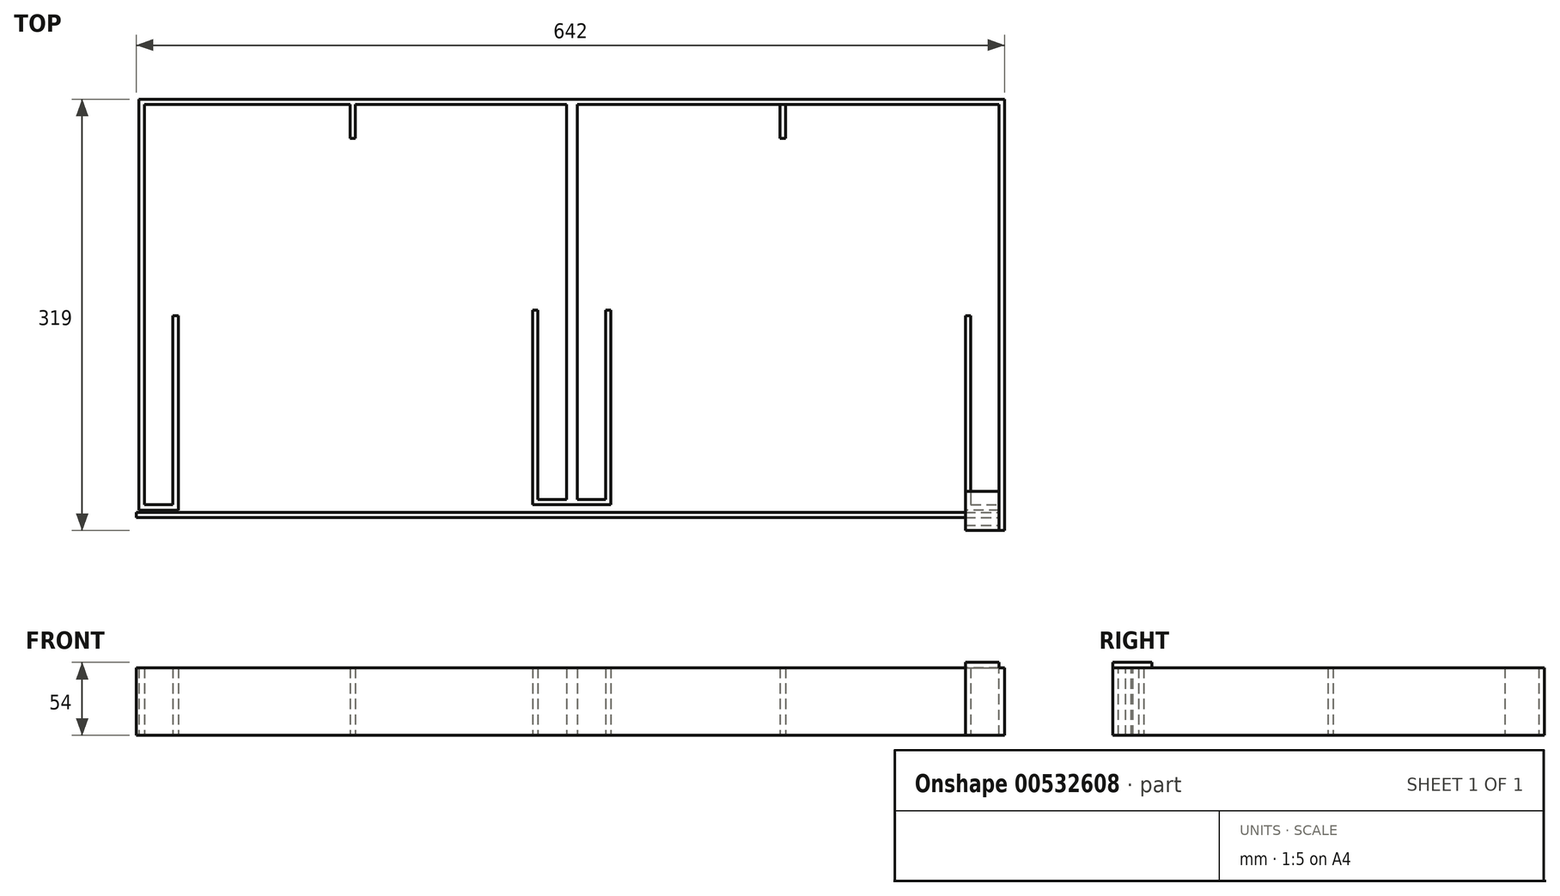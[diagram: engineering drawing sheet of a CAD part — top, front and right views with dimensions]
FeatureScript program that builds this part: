
annotation { "Feature Type Name" : "Feature", "Feature Type Description" : "" }
export const myFeature = defineFeature(function(context is Context, id is Id, definition is map)
    precondition{}
    {
        {
            var Q0;
            Q0=qCreatedBy(makeId("Front.planeOp"),FACE);
            var sketch = newSketch(context, id + "F0", { "sketchPlane" : qUnion([Q0])});
            skLineSegment(sketch, "E0.bottom", {"start": v(320, 25) * mm, "end": v(-320, 25) * mm});
            skLineSegment(sketch, "E0.top", {"start": v(320, -25) * mm, "end": v(-320, -25) * mm});
            skLineSegment(sketch, "E0.left", {"start": v(320, 25) * mm, "end": v(320, -25) * mm});
            skLineSegment(sketch, "E0.right", {"start": v(-320, 25) * mm, "end": v(-320, -25) * mm});
            skPoint(sketch, "E0.middle", {"position": v(0, 0) * mm});
            skSolve(sketch);
        }
        {
            var Q0;
            Q0=makeQuery(id+"F0.imprint","IMPRINT",FACE,{"disambiguationData":[TD([[makeQuery(id+"F0.imprint","IMPRINT",EDGE,{"derivedFrom":sQuery(id+"F0.wireOp",EDGE,"E0.bottom")}),1.0]])]});
            extrude(context, id + "F1", {"entities" : qUnion([Q0]), "depth" : 4 * mm, "offsetDistance" : 25 * mm});
        }
        {
            var Q0;
            Q0=makeQuery(id+"F1.opExtrude","CAP_FACE",FACE,{"disambiguationData":[OSD([sQuery(id+"F0.wireOp",EDGE,"E0.bottom"),sQuery(id+"F0.wireOp",EDGE,"E0.top"),sQuery(id+"F0.wireOp",EDGE,"E0.left"),sQuery(id+"F0.wireOp",EDGE,"E0.right")])],"isStart":false});
            var sketch = newSketch(context, id + "F2", { "sketchPlane" : qUnion([Q0])});
            skLineSegment(sketch, "E1.bottom", {"start": v(-320, 25) * mm, "end": v(-316, 25) * mm});
            skLineSegment(sketch, "E1.top", {"start": v(-320, -25) * mm, "end": v(-316, -25) * mm});
            skLineSegment(sketch, "E1.left", {"start": v(-320, 25) * mm, "end": v(-320, -25) * mm});
            skLineSegment(sketch, "E1.right", {"start": v(-316, 25) * mm, "end": v(-316, -25) * mm});
            skSolve(sketch);
        }
        {
            var Q0;
            Q0=qSketchRegion(id+"F2",true);
            extrude(context, id + "F3", {"entities" : qUnion([Q0]), "operationType" : NewBodyOperationType.ADD, "depth" : 300 * mm, "offsetDistance" : 25 * mm});
        }
        {
            var Q0;
            Q0=makeQuery(id+"F1.opExtrude","CAP_FACE",FACE,{"disambiguationData":[OSD([sQuery(id+"F0.wireOp",EDGE,"E0.bottom"),sQuery(id+"F0.wireOp",EDGE,"E0.top"),sQuery(id+"F0.wireOp",EDGE,"E0.left"),sQuery(id+"F0.wireOp",EDGE,"E0.right")])],"isStart":false});
            var sketch = newSketch(context, id + "F4", { "sketchPlane" : qUnion([Q0])});
            skLineSegment(sketch, "E2.bottom", {"start": v(320, -25) * mm, "end": v(316, -25) * mm});
            skLineSegment(sketch, "E2.top", {"start": v(320, 25) * mm, "end": v(316, 25) * mm});
            skLineSegment(sketch, "E2.left", {"start": v(320, -25) * mm, "end": v(320, 25) * mm});
            skLineSegment(sketch, "E2.right", {"start": v(316, -25) * mm, "end": v(316, 25) * mm});
            skSolve(sketch);
        }
        {
            var Q0;
            Q0=qSketchRegion(id+"F4",true);
            extrude(context, id + "F5", {"entities" : qUnion([Q0]), "operationType" : NewBodyOperationType.ADD, "depth" : 300 * mm, "offsetDistance" : 25 * mm});
        }
        {
            var Q0;
            Q0=makeQuery(id+"F3.opExtrude","SWEPT_FACE",FACE,{"disambiguationData":[OSD([sQuery(id+"F2.wireOp",EDGE,"E1.right")])]});
            var sketch = newSketch(context, id + "F6", { "sketchPlane" : qUnion([Q0])});
            skLineSegment(sketch, "E3.bottom", {"start": v(-304, 25) * mm, "end": v(-300, 25) * mm});
            skLineSegment(sketch, "E3.top", {"start": v(-304, -25) * mm, "end": v(-300, -25) * mm});
            skLineSegment(sketch, "E3.left", {"start": v(-304, 25) * mm, "end": v(-304, -25) * mm});
            skLineSegment(sketch, "E3.right", {"start": v(-300, 25) * mm, "end": v(-300, -25) * mm});
            skSolve(sketch);
        }
        {
            var Q0;
            Q0=qSketchRegion(id+"F6",true);
            extrude(context, id + "F7", {"entities" : qUnion([Q0]), "operationType" : NewBodyOperationType.ADD, "depth" : 25 * mm, "offsetDistance" : 25 * mm});
        }
        {
            var Q0;
            Q0=makeQuery(id+"F5.opExtrude","SWEPT_FACE",FACE,{"disambiguationData":[OSD([sQuery(id+"F4.wireOp",EDGE,"E2.right")])]});
            var sketch = newSketch(context, id + "F8", { "sketchPlane" : qUnion([Q0])});
            skLineSegment(sketch, "E4.bottom", {"start": v(304, 25) * mm, "end": v(300, 25) * mm});
            skLineSegment(sketch, "E4.top", {"start": v(304, -25) * mm, "end": v(300, -25) * mm});
            skLineSegment(sketch, "E4.left", {"start": v(304, 25) * mm, "end": v(304, -25) * mm});
            skLineSegment(sketch, "E4.right", {"start": v(300, 25) * mm, "end": v(300, -25) * mm});
            skSolve(sketch);
        }
        {
            var Q0;
            Q0=qSketchRegion(id+"F8",true);
            extrude(context, id + "F9", {"entities" : qUnion([Q0]), "operationType" : NewBodyOperationType.ADD, "depth" : 25 * mm, "offsetDistance" : 25 * mm});
        }
        {
            var Q0;
            Q0=qCreatedBy(makeId("Front.planeOp"),FACE);
            var sketch = newSketch(context, id + "F10", { "sketchPlane" : qUnion([Q0])});
            skLineSegment(sketch, "E5.bottom", {"start": v(4, 25) * mm, "end": v(-4, 25) * mm});
            skLineSegment(sketch, "E5.top", {"start": v(4, -25) * mm, "end": v(-4, -25) * mm});
            skLineSegment(sketch, "E5.left", {"start": v(4, 25) * mm, "end": v(4, -25) * mm});
            skLineSegment(sketch, "E5.right", {"start": v(-4, 25) * mm, "end": v(-4, -25) * mm});
            skPoint(sketch, "E5.middle", {"position": v(0, 0) * mm});
            skSolve(sketch);
        }
        {
            var Q0;
            Q0=qSketchRegion(id+"F10",true);
            extrude(context, id + "F11", {"entities" : qUnion([Q0]), "operationType" : NewBodyOperationType.ADD, "depth" : 300 * mm, "offsetDistance" : 25 * mm});
        }
        {
            var Q0;
            {var subQ0=sQuery(id+"F0.wireOp",EDGE,"E0.bottom");var subQ1=sQuery(id+"F0.wireOp",EDGE,"E0.top");Q0=makeQuery(id+"F11.boolean.opBoolean","SPLIT",FACE,{"disambiguationData":[TD([makeQuery(id+"F3.opExtrude","SWEPT_FACE",FACE,{"disambiguationData":[OSD([sQuery(id+"F2.wireOp",EDGE,"E1.right")])]})])],"derivedFrom":makeQuery(id+"F1.opExtrude","CAP_FACE",FACE,{"disambiguationData":[OSD([subQ0,subQ1,sQuery(id+"F0.wireOp",EDGE,"E0.left"),sQuery(id+"F0.wireOp",EDGE,"E0.right")])],"isStart":false})});}
            var sketch = newSketch(context, id + "F12", { "sketchPlane" : qUnion([Q0])});
            skLineSegment(sketch, "E6.bottom", {"start": v(-160, 25) * mm, "end": v(-164, 25) * mm});
            skLineSegment(sketch, "E6.top", {"start": v(-160, -25) * mm, "end": v(-164, -25) * mm});
            skLineSegment(sketch, "E6.left", {"start": v(-160, 25) * mm, "end": v(-160, -25) * mm});
            skLineSegment(sketch, "E6.right", {"start": v(-164, 25) * mm, "end": v(-164, -25) * mm});
            skSolve(sketch);
        }
        {
            var Q0;
            Q0=makeQuery(id+"F12.imprint","IMPRINT",FACE,{"disambiguationData":[TD([[makeQuery(id+"F12.imprint","IMPRINT",EDGE,{"derivedFrom":sQuery(id+"F12.wireOp",EDGE,"E6.bottom")}),1.0]])]});
            extrude(context, id + "F13", {"entities" : qUnion([Q0]), "operationType" : NewBodyOperationType.ADD, "depth" : 25 * mm, "offsetDistance" : 25 * mm});
        }
        {
            var Q0;
            Q0=makeQuery(id+"F11.opExtrude","SWEPT_FACE",FACE,{"disambiguationData":[OSD([sQuery(id+"F10.wireOp",EDGE,"E5.right")])]});
            var sketch = newSketch(context, id + "F14", { "sketchPlane" : qUnion([Q0])});
            skLineSegment(sketch, "E7.bottom", {"start": v(300, 25) * mm, "end": v(296, 25) * mm});
            skLineSegment(sketch, "E7.top", {"start": v(300, -25) * mm, "end": v(296, -25) * mm});
            skLineSegment(sketch, "E7.left", {"start": v(300, 25) * mm, "end": v(300, -25) * mm});
            skLineSegment(sketch, "E7.right", {"start": v(296, 25) * mm, "end": v(296, -25) * mm});
            skSolve(sketch);
        }
        {
            var Q0;
            Q0=qSketchRegion(id+"F14",true);
            extrude(context, id + "F15", {"entities" : qUnion([Q0]), "operationType" : NewBodyOperationType.ADD, "depth" : 25 * mm, "offsetDistance" : 25 * mm});
        }
        {
            var Q0;
            Q0=makeQuery(id+"F7.opExtrude","SWEPT_FACE",FACE,{"disambiguationData":[OSD([sQuery(id+"F6.wireOp",EDGE,"E3.right")])]});
            var sketch = newSketch(context, id + "F16", { "sketchPlane" : qUnion([Q0])});
            skLineSegment(sketch, "E8.bottom", {"start": v(291, 25) * mm, "end": v(295, 25) * mm});
            skLineSegment(sketch, "E8.top", {"start": v(291, -25) * mm, "end": v(295, -25) * mm});
            skLineSegment(sketch, "E8.left", {"start": v(291, 25) * mm, "end": v(291, -25) * mm});
            skLineSegment(sketch, "E8.right", {"start": v(295, 25) * mm, "end": v(295, -25) * mm});
            skSolve(sketch);
        }
        {
            var Q0;
            Q0=qSketchRegion(id+"F16",true);
            extrude(context, id + "F17", {"entities" : qUnion([Q0]), "operationType" : NewBodyOperationType.ADD, "depth" : 140 * mm, "offsetDistance" : 25 * mm});
        }
        {
            var Q0;
            Q0=makeQuery(id+"F15.opExtrude","SWEPT_FACE",FACE,{"disambiguationData":[OSD([sQuery(id+"F14.wireOp",EDGE,"E7.right")])]});
            var sketch = newSketch(context, id + "F18", { "sketchPlane" : qUnion([Q0])});
            skLineSegment(sketch, "E9.bottom", {"start": v(29, 25) * mm, "end": v(25, 25) * mm});
            skLineSegment(sketch, "E9.top", {"start": v(29, -25) * mm, "end": v(25, -25) * mm});
            skLineSegment(sketch, "E9.left", {"start": v(29, 25) * mm, "end": v(29, -25) * mm});
            skLineSegment(sketch, "E9.right", {"start": v(25, 25) * mm, "end": v(25, -25) * mm});
            skSolve(sketch);
        }
        {
            var Q0;
            Q0=qSketchRegion(id+"F18",true);
            extrude(context, id + "F19", {"entities" : qUnion([Q0]), "operationType" : NewBodyOperationType.ADD, "depth" : 140 * mm, "offsetDistance" : 25 * mm});
        }
        {
            var Q0;
            Q0=makeQuery(id+"F19.boolean.opBoolean","MERGE",FACE,{"derivedFrom":[makeQuery(id+"F17.boolean.opBoolean","MERGE",FACE,{"derivedFrom":[makeQuery(id+"F15.boolean.opBoolean","MERGE",FACE,{"derivedFrom":[makeQuery(id+"F13.boolean.opBoolean","MERGE",FACE,{"derivedFrom":[makeQuery(id+"F11.boolean.opBoolean","MERGE",FACE,{"derivedFrom":[makeQuery(id+"F9.boolean.opBoolean","MERGE",FACE,{"derivedFrom":[makeQuery(id+"F7.boolean.opBoolean","MERGE",FACE,{"derivedFrom":[makeQuery(id+"F5.boolean.opBoolean","MERGE",FACE,{"derivedFrom":[makeQuery(id+"F3.boolean.opBoolean","MERGE",FACE,{"derivedFrom":[makeQuery(id+"F1.opExtrude","SWEPT_FACE",FACE,{"disambiguationData":[OSD([sQuery(id+"F0.wireOp",EDGE,"E0.bottom")])]}),makeQuery(id+"F3.opExtrude","SWEPT_FACE",FACE,{"disambiguationData":[OSD([sQuery(id+"F2.wireOp",EDGE,"E1.bottom")])]})]}),makeQuery(id+"F5.opExtrude","SWEPT_FACE",FACE,{"disambiguationData":[OSD([sQuery(id+"F4.wireOp",EDGE,"E2.top")])]})]}),makeQuery(id+"F7.opExtrude","SWEPT_FACE",FACE,{"disambiguationData":[OSD([sQuery(id+"F6.wireOp",EDGE,"E3.bottom")])]})]}),makeQuery(id+"F9.opExtrude","SWEPT_FACE",FACE,{"disambiguationData":[OSD([sQuery(id+"F8.wireOp",EDGE,"E4.bottom")])]})]}),makeQuery(id+"F11.opExtrude","SWEPT_FACE",FACE,{"disambiguationData":[OSD([sQuery(id+"F10.wireOp",EDGE,"E5.bottom")])]})]}),makeQuery(id+"F13.opExtrude","SWEPT_FACE",FACE,{"disambiguationData":[OSD([sQuery(id+"F12.wireOp",EDGE,"E6.bottom")])]})]}),makeQuery(id+"F15.opExtrude","SWEPT_FACE",FACE,{"disambiguationData":[OSD([sQuery(id+"F14.wireOp",EDGE,"E7.bottom")])]})]}),makeQuery(id+"F17.opExtrude","SWEPT_FACE",FACE,{"disambiguationData":[OSD([sQuery(id+"F16.wireOp",EDGE,"E8.bottom")])]})]}),makeQuery(id+"F19.opExtrude","SWEPT_FACE",FACE,{"disambiguationData":[OSD([sQuery(id+"F18.wireOp",EDGE,"E9.bottom")])]})]});
            var sketch = newSketch(context, id + "F20", { "sketchPlane" : qUnion([Q0])});
            skArc(sketch, "E10", {"start": v(-25, -156) * mm, "mid": v(-161.91, -28.95) * mm, "end": v(-295, -160) * mm});
            skArc(sketch, "E11", {"start": v(-29, -156) * mm, "mid": v(-161.91, -32.85) * mm, "end": v(-291, -160) * mm});
            skSolve(sketch);
        }
        {
            var Q0;
            Q0=sQuery(id+"F20.wireOp",EDGE,"E11");
            var Q1;
            Q1=sQuery(id+"F20.wireOp",EDGE,"E10");
            extrude(context, id + "F21", {"bodyType" : ToolBodyType.SURFACE, "surfaceEntities" : qUnion([Q0, Q1]), "oppositeDirection" : true, "depth" : 50 * mm, "offsetDistance" : 25 * mm});
        }
        {
            var Q0;
            Q0=makeQuery(id+"F11.opExtrude","SWEPT_FACE",FACE,{"disambiguationData":[OSD([sQuery(id+"F10.wireOp",EDGE,"E5.left")])]});
            var sketch = newSketch(context, id + "F22", { "sketchPlane" : qUnion([Q0])});
            skLineSegment(sketch, "E12.bottom", {"start": v(-300, 25) * mm, "end": v(-296, 25) * mm});
            skLineSegment(sketch, "E12.top", {"start": v(-300, -25) * mm, "end": v(-296, -25) * mm});
            skLineSegment(sketch, "E12.left", {"start": v(-300, 25) * mm, "end": v(-300, -25) * mm});
            skLineSegment(sketch, "E12.right", {"start": v(-296, 25) * mm, "end": v(-296, -25) * mm});
            skSolve(sketch);
        }
        {
            var Q0;
            Q0=qSketchRegion(id+"F22",true);
            extrude(context, id + "F23", {"entities" : qUnion([Q0]), "operationType" : NewBodyOperationType.ADD, "depth" : 25 * mm, "offsetDistance" : 25 * mm});
        }
        {
            var Q0;
            Q0=makeQuery(id+"F23.opExtrude","SWEPT_FACE",FACE,{"disambiguationData":[OSD([sQuery(id+"F22.wireOp",EDGE,"E12.right")])]});
            var sketch = newSketch(context, id + "F24", { "sketchPlane" : qUnion([Q0])});
            skLineSegment(sketch, "E13.bottom", {"start": v(-29, 25) * mm, "end": v(-25, 25) * mm});
            skLineSegment(sketch, "E13.top", {"start": v(-29, -25) * mm, "end": v(-25, -25) * mm});
            skLineSegment(sketch, "E13.left", {"start": v(-29, 25) * mm, "end": v(-29, -25) * mm});
            skLineSegment(sketch, "E13.right", {"start": v(-25, 25) * mm, "end": v(-25, -25) * mm});
            skSolve(sketch);
        }
        {
            var Q0;
            Q0=qSketchRegion(id+"F24",true);
            extrude(context, id + "F25", {"entities" : qUnion([Q0]), "operationType" : NewBodyOperationType.ADD, "depth" : 140 * mm, "offsetDistance" : 25 * mm});
        }
        {
            var Q0;
            Q0=makeQuery(id+"F9.opExtrude","SWEPT_FACE",FACE,{"disambiguationData":[OSD([sQuery(id+"F8.wireOp",EDGE,"E4.right")])]});
            var sketch = newSketch(context, id + "F26", { "sketchPlane" : qUnion([Q0])});
            skLineSegment(sketch, "E14.bottom", {"start": v(-291, 25) * mm, "end": v(-295, 25) * mm});
            skLineSegment(sketch, "E14.top", {"start": v(-291, -25) * mm, "end": v(-295, -25) * mm});
            skLineSegment(sketch, "E14.left", {"start": v(-291, 25) * mm, "end": v(-291, -25) * mm});
            skLineSegment(sketch, "E14.right", {"start": v(-295, 25) * mm, "end": v(-295, -25) * mm});
            skSolve(sketch);
        }
        {
            var Q0;
            Q0=qSketchRegion(id+"F26",true);
            extrude(context, id + "F27", {"entities" : qUnion([Q0]), "operationType" : NewBodyOperationType.ADD, "depth" : 140 * mm, "offsetDistance" : 25 * mm});
        }
        {
            var Q0;
            Q0=makeQuery(id+"F27.boolean.opBoolean","MERGE",FACE,{"derivedFrom":[makeQuery(id+"F25.boolean.opBoolean","MERGE",FACE,{"derivedFrom":[makeQuery(id+"F23.boolean.opBoolean","MERGE",FACE,{"derivedFrom":[makeQuery(id+"F19.boolean.opBoolean","MERGE",FACE,{"derivedFrom":[makeQuery(id+"F17.boolean.opBoolean","MERGE",FACE,{"derivedFrom":[makeQuery(id+"F15.boolean.opBoolean","MERGE",FACE,{"derivedFrom":[makeQuery(id+"F13.boolean.opBoolean","MERGE",FACE,{"derivedFrom":[makeQuery(id+"F11.boolean.opBoolean","MERGE",FACE,{"derivedFrom":[makeQuery(id+"F9.boolean.opBoolean","MERGE",FACE,{"derivedFrom":[makeQuery(id+"F7.boolean.opBoolean","MERGE",FACE,{"derivedFrom":[makeQuery(id+"F5.boolean.opBoolean","MERGE",FACE,{"derivedFrom":[makeQuery(id+"F3.boolean.opBoolean","MERGE",FACE,{"derivedFrom":[makeQuery(id+"F1.opExtrude","SWEPT_FACE",FACE,{"disambiguationData":[OSD([sQuery(id+"F0.wireOp",EDGE,"E0.top")])]}),makeQuery(id+"F3.opExtrude","SWEPT_FACE",FACE,{"disambiguationData":[OSD([sQuery(id+"F2.wireOp",EDGE,"E1.top")])]})]}),makeQuery(id+"F5.opExtrude","SWEPT_FACE",FACE,{"disambiguationData":[OSD([sQuery(id+"F4.wireOp",EDGE,"E2.bottom")])]})]}),makeQuery(id+"F7.opExtrude","SWEPT_FACE",FACE,{"disambiguationData":[OSD([sQuery(id+"F6.wireOp",EDGE,"E3.top")])]})]}),makeQuery(id+"F9.opExtrude","SWEPT_FACE",FACE,{"disambiguationData":[OSD([sQuery(id+"F8.wireOp",EDGE,"E4.top")])]})]}),makeQuery(id+"F11.opExtrude","SWEPT_FACE",FACE,{"disambiguationData":[OSD([sQuery(id+"F10.wireOp",EDGE,"E5.top")])]})]}),makeQuery(id+"F13.opExtrude","SWEPT_FACE",FACE,{"disambiguationData":[OSD([sQuery(id+"F12.wireOp",EDGE,"E6.top")])]})]}),makeQuery(id+"F15.opExtrude","SWEPT_FACE",FACE,{"disambiguationData":[OSD([sQuery(id+"F14.wireOp",EDGE,"E7.top")])]})]}),makeQuery(id+"F17.opExtrude","SWEPT_FACE",FACE,{"disambiguationData":[OSD([sQuery(id+"F16.wireOp",EDGE,"E8.top")])]})]}),makeQuery(id+"F19.opExtrude","SWEPT_FACE",FACE,{"disambiguationData":[OSD([sQuery(id+"F18.wireOp",EDGE,"E9.top")])]})]}),makeQuery(id+"F23.opExtrude","SWEPT_FACE",FACE,{"disambiguationData":[OSD([sQuery(id+"F22.wireOp",EDGE,"E12.top")])]})]}),makeQuery(id+"F25.opExtrude","SWEPT_FACE",FACE,{"disambiguationData":[OSD([sQuery(id+"F24.wireOp",EDGE,"E13.top")])]})]}),makeQuery(id+"F27.opExtrude","SWEPT_FACE",FACE,{"disambiguationData":[OSD([sQuery(id+"F26.wireOp",EDGE,"E14.top")])]})]});
            var sketch = newSketch(context, id + "F28", { "sketchPlane" : qUnion([Q0])});
            skLineSegment(sketch, "E15", {"start": v(4, 4) * mm, "end": v(154, 4) * mm});
            skLineSegment(sketch, "E16.bottom", {"start": v(154, 4) * mm, "end": v(158, 4) * mm});
            skLineSegment(sketch, "E16.top", {"start": v(154, 29) * mm, "end": v(158, 29) * mm});
            skLineSegment(sketch, "E16.left", {"start": v(154, 4) * mm, "end": v(154, 29) * mm});
            skLineSegment(sketch, "E16.right", {"start": v(158, 4) * mm, "end": v(158, 29) * mm});
            skSolve(sketch);
        }
        {
            var Q0;
            Q0=qSketchRegion(id+"F28",true);
            extrude(context, id + "F29", {"entities" : qUnion([Q0]), "oppositeDirection" : true, "depth" : 50 * mm, "offsetDistance" : 25 * mm});
        }
        {
            var Q0;
            Q0=makeQuery(id+"F21.opExtrude","SWEPT_BODY",BODY,{"disambiguationData":[OSD([sQuery(id+"F20.wireOp",EDGE,"E10")])]});
            var Q1;
            Q1=makeQuery(id+"F21.opExtrude","SWEPT_BODY",BODY,{"disambiguationData":[OSD([sQuery(id+"F20.wireOp",EDGE,"E11")])]});
            var Q2;
            Q2=qCreatedBy(makeId("Right.planeOp"),FACE);
            mirror(context, id + "F30", {"entities" : qUnion([Q0, Q1]), "mirrorPlane" : qUnion([Q2])});
        }
        {
            var Q0;
            Q0=makeQuery(id+"F9.boolean.opBoolean","MERGE",FACE,{"derivedFrom":[makeQuery(id+"F5.opExtrude","CAP_FACE",FACE,{"disambiguationData":[OSD([sQuery(id+"F4.wireOp",EDGE,"E2.bottom"),sQuery(id+"F4.wireOp",EDGE,"E2.top"),sQuery(id+"F4.wireOp",EDGE,"E2.left"),sQuery(id+"F4.wireOp",EDGE,"E2.right")])],"isStart":false}),makeQuery(id+"F9.opExtrude","SWEPT_FACE",FACE,{"disambiguationData":[OSD([sQuery(id+"F8.wireOp",EDGE,"E4.left")])]})]});
            var sketch = newSketch(context, id + "F31", { "sketchPlane" : qUnion([Q0])});
            skLineSegment(sketch, "E17.bottom", {"start": v(320, -25) * mm, "end": v(316, -25) * mm});
            skLineSegment(sketch, "E17.top", {"start": v(320, 25) * mm, "end": v(316, 25) * mm});
            skLineSegment(sketch, "E17.left", {"start": v(320, -25) * mm, "end": v(320, 25) * mm});
            skLineSegment(sketch, "E17.right", {"start": v(316, -25) * mm, "end": v(316, 25) * mm});
            skSolve(sketch);
        }
        {
            var Q0;
            Q0=qSketchRegion(id+"F31",true);
            extrude(context, id + "F32", {"entities" : qUnion([Q0]), "operationType" : NewBodyOperationType.ADD, "depth" : 15 * mm, "offsetDistance" : 25 * mm});
        }
        {
            var Q0;
            Q0=makeQuery(id+"F32.opExtrude","SWEPT_FACE",FACE,{"disambiguationData":[OSD([sQuery(id+"F31.wireOp",EDGE,"E17.right")])]});
            var sketch = newSketch(context, id + "F33", { "sketchPlane" : qUnion([Q0])});
            skLineSegment(sketch, "E18.bottom", {"start": v(319, -25) * mm, "end": v(315, -25) * mm});
            skLineSegment(sketch, "E18.top", {"start": v(319, 25) * mm, "end": v(315, 25) * mm});
            skLineSegment(sketch, "E18.left", {"start": v(319, -25) * mm, "end": v(319, 25) * mm});
            skLineSegment(sketch, "E18.right", {"start": v(315, -25) * mm, "end": v(315, 25) * mm});
            skSolve(sketch);
        }
        {
            var Q0;
            Q0=qSketchRegion(id+"F33",true);
            extrude(context, id + "F34", {"entities" : qUnion([Q0]), "operationType" : NewBodyOperationType.ADD, "depth" : 25 * mm, "offsetDistance" : 25 * mm});
        }
        {
            var Q0;
            Q0=makeQuery(id+"F34.boolean.opBoolean","MERGE",FACE,{"derivedFrom":[makeQuery(id+"F32.boolean.opBoolean","MERGE",FACE,{"derivedFrom":[makeQuery(id+"F27.boolean.opBoolean","MERGE",FACE,{"derivedFrom":[makeQuery(id+"F25.boolean.opBoolean","MERGE",FACE,{"derivedFrom":[makeQuery(id+"F23.boolean.opBoolean","MERGE",FACE,{"derivedFrom":[makeQuery(id+"F19.boolean.opBoolean","MERGE",FACE,{"derivedFrom":[makeQuery(id+"F17.boolean.opBoolean","MERGE",FACE,{"derivedFrom":[makeQuery(id+"F15.boolean.opBoolean","MERGE",FACE,{"derivedFrom":[makeQuery(id+"F13.boolean.opBoolean","MERGE",FACE,{"derivedFrom":[makeQuery(id+"F11.boolean.opBoolean","MERGE",FACE,{"derivedFrom":[makeQuery(id+"F9.boolean.opBoolean","MERGE",FACE,{"derivedFrom":[makeQuery(id+"F7.boolean.opBoolean","MERGE",FACE,{"derivedFrom":[makeQuery(id+"F5.boolean.opBoolean","MERGE",FACE,{"derivedFrom":[makeQuery(id+"F3.boolean.opBoolean","MERGE",FACE,{"derivedFrom":[makeQuery(id+"F1.opExtrude","SWEPT_FACE",FACE,{"disambiguationData":[OSD([sQuery(id+"F0.wireOp",EDGE,"E0.bottom")])]}),makeQuery(id+"F3.opExtrude","SWEPT_FACE",FACE,{"disambiguationData":[OSD([sQuery(id+"F2.wireOp",EDGE,"E1.bottom")])]})]}),makeQuery(id+"F5.opExtrude","SWEPT_FACE",FACE,{"disambiguationData":[OSD([sQuery(id+"F4.wireOp",EDGE,"E2.top")])]})]}),makeQuery(id+"F7.opExtrude","SWEPT_FACE",FACE,{"disambiguationData":[OSD([sQuery(id+"F6.wireOp",EDGE,"E3.bottom")])]})]}),makeQuery(id+"F9.opExtrude","SWEPT_FACE",FACE,{"disambiguationData":[OSD([sQuery(id+"F8.wireOp",EDGE,"E4.bottom")])]})]}),makeQuery(id+"F11.opExtrude","SWEPT_FACE",FACE,{"disambiguationData":[OSD([sQuery(id+"F10.wireOp",EDGE,"E5.bottom")])]})]}),makeQuery(id+"F13.opExtrude","SWEPT_FACE",FACE,{"disambiguationData":[OSD([sQuery(id+"F12.wireOp",EDGE,"E6.bottom")])]})]}),makeQuery(id+"F15.opExtrude","SWEPT_FACE",FACE,{"disambiguationData":[OSD([sQuery(id+"F14.wireOp",EDGE,"E7.bottom")])]})]}),makeQuery(id+"F17.opExtrude","SWEPT_FACE",FACE,{"disambiguationData":[OSD([sQuery(id+"F16.wireOp",EDGE,"E8.bottom")])]})]}),makeQuery(id+"F19.opExtrude","SWEPT_FACE",FACE,{"disambiguationData":[OSD([sQuery(id+"F18.wireOp",EDGE,"E9.bottom")])]})]}),makeQuery(id+"F23.opExtrude","SWEPT_FACE",FACE,{"disambiguationData":[OSD([sQuery(id+"F22.wireOp",EDGE,"E12.bottom")])]})]}),makeQuery(id+"F25.opExtrude","SWEPT_FACE",FACE,{"disambiguationData":[OSD([sQuery(id+"F24.wireOp",EDGE,"E13.bottom")])]})]}),makeQuery(id+"F27.opExtrude","SWEPT_FACE",FACE,{"disambiguationData":[OSD([sQuery(id+"F26.wireOp",EDGE,"E14.bottom")])]})]}),makeQuery(id+"F32.opExtrude","SWEPT_FACE",FACE,{"disambiguationData":[OSD([sQuery(id+"F31.wireOp",EDGE,"E17.top")])]})]}),makeQuery(id+"F34.opExtrude","SWEPT_FACE",FACE,{"disambiguationData":[OSD([sQuery(id+"F33.wireOp",EDGE,"E18.top")])]})]});
            var sketch = newSketch(context, id + "F35", { "sketchPlane" : qUnion([Q0])});
            skLineSegment(sketch, "E19.bottom", {"start": v(291, -319) * mm, "end": v(316, -319) * mm});
            skLineSegment(sketch, "E19.top", {"start": v(291, -315) * mm, "end": v(316, -315) * mm});
            skLineSegment(sketch, "E19.left", {"start": v(291, -319) * mm, "end": v(291, -315) * mm});
            skLineSegment(sketch, "E19.right", {"start": v(316, -319) * mm, "end": v(316, -315) * mm});
            skSolve(sketch);
        }
        {
            var Q0;
            Q0=qSketchRegion(id+"F35",true);
            extrude(context, id + "F36", {"entities" : qUnion([Q0]), "operationType" : NewBodyOperationType.ADD, "depth" : 4 * mm, "offsetDistance" : 25 * mm});
        }
        {
            var Q0;
            Q0=makeQuery(id+"F36.boolean.opBoolean","MERGE",FACE,{"derivedFrom":[makeQuery(id+"F34.opExtrude","SWEPT_FACE",FACE,{"disambiguationData":[OSD([sQuery(id+"F33.wireOp",EDGE,"E18.right")])]}),makeQuery(id+"F36.opExtrude","SWEPT_FACE",FACE,{"disambiguationData":[OSD([sQuery(id+"F35.wireOp",EDGE,"E19.top")])]})]});
            var sketch = newSketch(context, id + "F37", { "sketchPlane" : qUnion([Q0])});
            skLineSegment(sketch, "E20.bottom", {"start": v(-291, 29) * mm, "end": v(-316, 29) * mm});
            skLineSegment(sketch, "E20.top", {"start": v(-291, 25.1) * mm, "end": v(-316, 25.1) * mm});
            skLineSegment(sketch, "E20.left", {"start": v(-291, 29) * mm, "end": v(-291, 25.1) * mm});
            skLineSegment(sketch, "E20.right", {"start": v(-316, 29) * mm, "end": v(-316, 25.1) * mm});
            skSolve(sketch);
        }
        {
            var Q0;
            Q0=qSketchRegion(id+"F37",true);
            extrude(context, id + "F38", {"entities" : qUnion([Q0]), "operationType" : NewBodyOperationType.ADD, "depth" : 25 * mm, "offsetDistance" : 25 * mm});
        }
        {
            var Q0;
            Q0=makeQuery(id+"F32.opExtrude","SWEPT_FACE",FACE,{"disambiguationData":[OSD([sQuery(id+"F31.wireOp",EDGE,"E17.right")])]});
            var sketch = newSketch(context, id + "F39", { "sketchPlane" : qUnion([Q0])});
            skLineSegment(sketch, "E21.bottom", {"start": v(309.5, -25) * mm, "end": v(305.5, -25) * mm});
            skLineSegment(sketch, "E21.top", {"start": v(309.5, 25) * mm, "end": v(305.5, 25) * mm});
            skLineSegment(sketch, "E21.left", {"start": v(309.5, -25) * mm, "end": v(309.5, 25) * mm});
            skLineSegment(sketch, "E21.right", {"start": v(305.5, -25) * mm, "end": v(305.5, 25) * mm});
            skSolve(sketch);
        }
        {
            var Q0;
            Q0=qSketchRegion(id+"F39",true);
            extrude(context, id + "F40", {"entities" : qUnion([Q0]), "operationType" : NewBodyOperationType.ADD, "depth" : 638 * mm, "offsetDistance" : 25 * mm});
        }
    });
